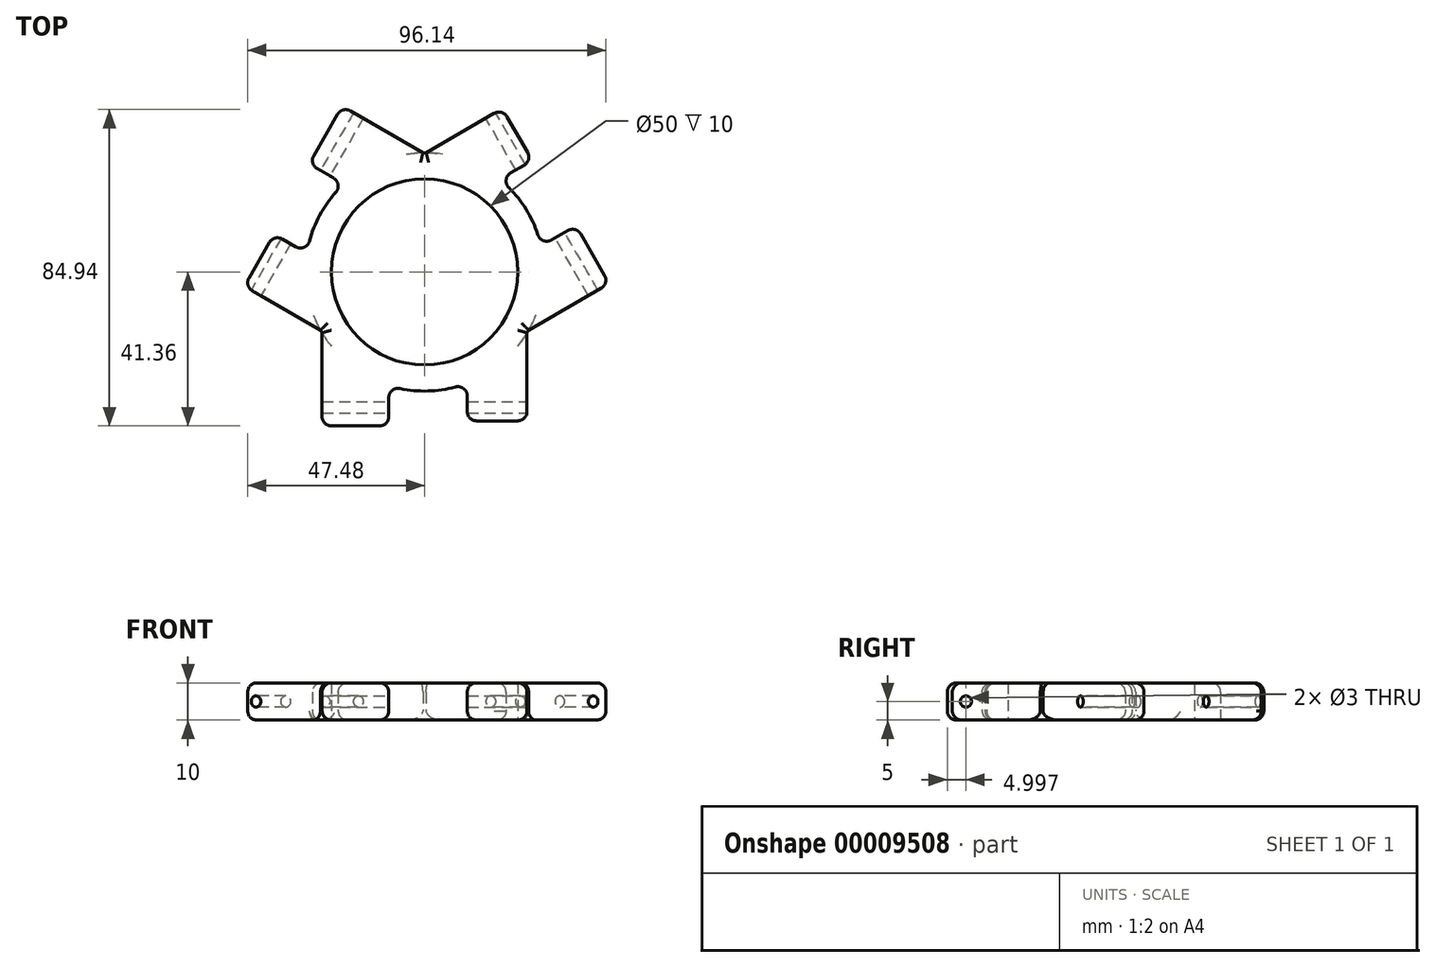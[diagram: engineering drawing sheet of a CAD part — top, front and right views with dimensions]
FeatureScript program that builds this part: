
annotation { "Feature Type Name" : "Feature", "Feature Type Description" : "" }
export const myFeature = defineFeature(function(context is Context, id is Id, definition is map)
    precondition{}
    {
        {
            var Q0;
            Q0=qCreatedBy(makeId("Top.planeOp"),FACE);
            var sketch = newSketch(context, id + "F0", { "sketchPlane" : qUnion([Q0])});
            skCircle(sketch, "E0", {"center": v(0, 0) * mm, "radius": 25 * mm});
            skCircle(sketch, "E1", {"center": v(0, 0) * mm, "radius": 32 * mm});
            skLineSegment(sketch, "E2", {"start": v(-9.6, -41.36) * mm, "end": v(-9.6, -30.53) * mm});
            skLineSegment(sketch, "E3", {"start": v(11.45, -29.88) * mm, "end": v(11.45, -40) * mm});
            skLineSegment(sketch, "E4", {"start": v(-27.5, -41.36) * mm, "end": v(-9.6, -41.36) * mm});
            skLineSegment(sketch, "E5", {"start": v(11.45, -40) * mm, "end": v(27.5, -40) * mm});
            skLineSegment(sketch, "E6", {"start": v(27.5, -40) * mm, "end": v(27.5, -16.36) * mm});
            skLineSegment(sketch, "E7", {"start": v(-27.5, -41.36) * mm, "end": v(-27.5, -16.36) * mm});
            skLineSegment(sketch, "E8.1.0", {"start": v(28.91, 29.92) * mm, "end": v(20.9, 43.82) * mm});
            skLineSegment(sketch, "E8.1.1", {"start": v(49.57, -3.13) * mm, "end": v(27.92, -15.63) * mm});
            skLineSegment(sketch, "E8.1.2", {"start": v(49.57, -3.13) * mm, "end": v(40.62, 12.37) * mm});
            skLineSegment(sketch, "E8.1.3", {"start": v(20.9, 43.82) * mm, "end": v(0.42, 32) * mm});
            skLineSegment(sketch, "E8.1.4", {"start": v(20.15, 24.86) * mm, "end": v(28.91, 29.92) * mm});
            skLineSegment(sketch, "E8.1.5", {"start": v(40.62, 12.37) * mm, "end": v(31.24, 6.95) * mm});
            skLineSegment(sketch, "E8.2.0", {"start": v(-40.37, 10.08) * mm, "end": v(-48.4, -3.82) * mm});
            skLineSegment(sketch, "E8.2.1", {"start": v(-22.07, 44.5) * mm, "end": v(-0.42, 32) * mm});
            skLineSegment(sketch, "E8.2.2", {"start": v(-22.07, 44.5) * mm, "end": v(-31.02, 29) * mm});
            skLineSegment(sketch, "E8.2.3", {"start": v(-48.4, -3.82) * mm, "end": v(-27.92, -15.63) * mm});
            skLineSegment(sketch, "E8.2.4", {"start": v(-31.6, 5.02) * mm, "end": v(-40.37, 10.08) * mm});
            skLineSegment(sketch, "E8.2.5", {"start": v(-31.02, 29) * mm, "end": v(-21.63, 23.58) * mm});
            skSolve(sketch);
        }
        {
            var Q0;
            Q0=makeQuery(id+"F0.imprint","IMPRINT",FACE,{"disambiguationData":[TD([[makeQuery(id+"F0.imprint","IMPRINT",EDGE,{"derivedFrom":sQuery(id+"F0.wireOp",EDGE,"E0")}),-1.0]])]});
            var Q1;
            Q1=makeQuery(id+"F0.imprint","IMPRINT",FACE,{"disambiguationData":[TD([[makeQuery(id+"F0.imprint","IMPRINT",EDGE,{"derivedFrom":sQuery(id+"F0.wireOp",EDGE,"E8.2.0")}),1.0]])]});
            var Q2;
            {var subQ1=sQuery(id+"F0.wireOp",EDGE,"E2");Q2=makeQuery(id+"F0.imprint","IMPRINT",FACE,{"disambiguationData":[TD([[makeQuery(id+"F0.imprint","IMPRINT",EDGE,{"derivedFrom":subQ1}),1.0]])]});}
            var Q3;
            {var subQ1=sQuery(id+"F0.wireOp",EDGE,"E8.2.1");Q3=makeQuery(id+"F0.imprint","IMPRINT",FACE,{"disambiguationData":[TD([[makeQuery(id+"F0.imprint","IMPRINT",EDGE,{"derivedFrom":subQ1}),-1.0]])]});}
            var Q4;
            Q4=makeQuery(id+"F0.imprint","IMPRINT",FACE,{"disambiguationData":[TD([[makeQuery(id+"F0.imprint","IMPRINT",EDGE,{"derivedFrom":sQuery(id+"F0.wireOp",EDGE,"E8.1.0")}),1.0]])]});
            var Q5;
            {var subQ1=sQuery(id+"F0.wireOp",EDGE,"E8.1.1");Q5=makeQuery(id+"F0.imprint","IMPRINT",FACE,{"disambiguationData":[TD([[makeQuery(id+"F0.imprint","IMPRINT",EDGE,{"derivedFrom":subQ1}),-1.0]])]});}
            var Q6;
            {var subQ0=sQuery(id+"F0.wireOp",EDGE,"E3");Q6=makeQuery(id+"F0.imprint","IMPRINT",FACE,{"disambiguationData":[TD([[makeQuery(id+"F0.imprint","IMPRINT",EDGE,{"derivedFrom":subQ0}),1.0]])]});}
            extrude(context, id + "F1", {"entities" : qUnion([Q0, Q1, Q2, Q3, Q4, Q5, Q6]), "depth" : 10 * mm});
        }
        {
            var Q0;
            Q0=makeQuery(id+"F1.opExtrude","SWEPT_FACE",FACE,{"disambiguationData":[OSD([sQuery(id+"F0.wireOp",EDGE,"E7")])]});
            var sketch = newSketch(context, id + "F2", { "sketchPlane" : qUnion([Q0])});
            skCircle(sketch, "E9", {"center": v(36.36, 5) * mm, "radius": 1.5 * mm});
            skSolve(sketch);
        }
        {
            var Q0;
            Q0 = qSketchRegion(id + "F2", true);
            extrude(context, id + "F3", {"entities" : qUnion([Q0]), "depth" : 5 * mm, "hasSecondDirection" : true, "secondDirectionOppositeDirection" : true, "secondDirectionDepth" : 60 * mm});
        }
        {
            var Q0;
            Q0=makeQuery(id+"F3.opExtrude","SWEPT_BODY",BODY,{"disambiguationData":[OSD([sQuery(id+"F2.wireOp",EDGE,"E9")])]});
            var Q1;
            Q1=makeQuery(id+"F1.opExtrude","SWEPT_FACE",FACE,{"disambiguationData":[OSD([sQuery(id+"F0.wireOp",EDGE,"E0")])]});
            circularPattern(context, id + "F4", {"entities" : qUnion([Q0]), "axis" : qUnion([Q1]), "angle" : 120 * degree, "instanceCount" : 3});
        }
        {
            var Q0;
            Q0=makeQuery(id+"F3.opExtrude","SWEPT_BODY",BODY,{"disambiguationData":[OSD([sQuery(id+"F2.wireOp",EDGE,"E9")])]});
            var Q1;
            Q1=makeQuery(id+"F4.opPattern","COPY",BODY,{"derivedFrom":makeQuery(id+"F3.opExtrude","SWEPT_BODY",BODY,{"disambiguationData":[OSD([sQuery(id+"F2.wireOp",EDGE,"E9")])]}),"instanceName":"2"});
            var Q2;
            Q2=makeQuery(id+"F4.opPattern","COPY",BODY,{"derivedFrom":makeQuery(id+"F3.opExtrude","SWEPT_BODY",BODY,{"disambiguationData":[OSD([sQuery(id+"F2.wireOp",EDGE,"E9")])]}),"instanceName":"1"});
            var Q3;
            Q3=makeQuery(id+"F1.opExtrude","SWEPT_BODY",BODY,{"disambiguationData":[OSD([sQuery(id+"F0.wireOp",EDGE,"E0"),sQuery(id+"F0.wireOp",EDGE,"E1"),sQuery(id+"F0.wireOp",EDGE,"E2"),sQuery(id+"F0.wireOp",EDGE,"E3"),sQuery(id+"F0.wireOp",EDGE,"E4"),sQuery(id+"F0.wireOp",EDGE,"E5"),sQuery(id+"F0.wireOp",EDGE,"E6"),sQuery(id+"F0.wireOp",EDGE,"E7"),sQuery(id+"F0.wireOp",EDGE,"E8.1.0"),sQuery(id+"F0.wireOp",EDGE,"E8.1.1"),sQuery(id+"F0.wireOp",EDGE,"E8.1.2"),sQuery(id+"F0.wireOp",EDGE,"E8.1.3"),sQuery(id+"F0.wireOp",EDGE,"E8.1.4"),sQuery(id+"F0.wireOp",EDGE,"E8.1.5"),sQuery(id+"F0.wireOp",EDGE,"E8.2.0"),sQuery(id+"F0.wireOp",EDGE,"E8.2.1"),sQuery(id+"F0.wireOp",EDGE,"E8.2.2"),sQuery(id+"F0.wireOp",EDGE,"E8.2.3"),sQuery(id+"F0.wireOp",EDGE,"E8.2.4"),sQuery(id+"F0.wireOp",EDGE,"E8.2.5")])]});
            booleanBodies(context, id + "F5", {"operationType" : BooleanOperationType.SUBTRACTION, "tools" : qUnion([Q0, Q1, Q2]), "targets" : qUnion([Q3])});
        }
        {
            var Q0;
            Q0=makeQuery(id+"F1.opExtrude","CAP_EDGE",EDGE,{"disambiguationData":[OSD([sQuery(id+"F0.wireOp",EDGE,"E8.2.3")])],"isStart":false});
            var Q1;
            Q1=makeQuery(id+"F1.opExtrude","CAP_EDGE",EDGE,{"disambiguationData":[OSD([sQuery(id+"F0.wireOp",EDGE,"E8.2.0")])],"isStart":false});
            var Q2;
            Q2=makeQuery(id+"F1.opExtrude","SWEPT_EDGE",EDGE,{"disambiguationData":[OSD([sQuery(id+"F0.wireOp",EDGE,"E8.2.0"),sQuery(id+"F0.wireOp",EDGE,"E8.2.3")])]});
            var Q3;
            Q3=makeQuery(id+"F1.opExtrude","CAP_EDGE",EDGE,{"disambiguationData":[OSD([sQuery(id+"F0.wireOp",EDGE,"E8.2.4")])],"isStart":false});
            var Q4;
            Q4=makeQuery(id+"F1.opExtrude","SWEPT_EDGE",EDGE,{"disambiguationData":[OSD([sQuery(id+"F0.wireOp",EDGE,"E8.2.0"),sQuery(id+"F0.wireOp",EDGE,"E8.2.4")])]});
            var Q5;
            Q5=makeQuery(id+"F1.opExtrude","CAP_EDGE",EDGE,{"disambiguationData":[OSD([sQuery(id+"F0.wireOp",EDGE,"E8.2.4")])],"isStart":true});
            var Q6;
            {var subQ0=sQuery(id+"F0.wireOp",EDGE,"E1");Q6=makeQuery(id+"F1.opExtrude","CAP_EDGE",EDGE,{"disambiguationData":[OSD([subQ0]),TDD([makeQuery(id+"F0.imprint","IMPRINT",EDGE,{"disambiguationData":[TD([[makeQuery(id+"F0.imprint","INTERSECT",VERTEX,{"derivedFrom":[subQ0,sQuery(id+"F0.wireOp",EDGE,"E8.2.4")]}),1.0]])],"derivedFrom":subQ0})])],"isStart":false});}
            var Q7;
            Q7=makeQuery(id+"F1.opExtrude","CAP_EDGE",EDGE,{"disambiguationData":[OSD([sQuery(id+"F0.wireOp",EDGE,"E8.2.5")])],"isStart":false});
            var Q8;
            Q8=makeQuery(id+"F1.opExtrude","CAP_EDGE",EDGE,{"disambiguationData":[OSD([sQuery(id+"F0.wireOp",EDGE,"E8.2.2")])],"isStart":false});
            var Q9;
            Q9=makeQuery(id+"F1.opExtrude","SWEPT_EDGE",EDGE,{"disambiguationData":[OSD([sQuery(id+"F0.wireOp",EDGE,"E8.2.2"),sQuery(id+"F0.wireOp",EDGE,"E8.2.5")])]});
            var Q10;
            Q10=makeQuery(id+"F1.opExtrude","SWEPT_EDGE",EDGE,{"disambiguationData":[OSD([sQuery(id+"F0.wireOp",EDGE,"E8.2.1"),sQuery(id+"F0.wireOp",EDGE,"E8.2.2")])]});
            var Q11;
            Q11=makeQuery(id+"F1.opExtrude","CAP_EDGE",EDGE,{"disambiguationData":[OSD([sQuery(id+"F0.wireOp",EDGE,"E8.2.1")])],"isStart":false});
            var Q12;
            Q12=makeQuery(id+"F1.opExtrude","CAP_EDGE",EDGE,{"disambiguationData":[OSD([sQuery(id+"F0.wireOp",EDGE,"E8.1.3")])],"isStart":false});
            var Q13;
            {var subQ0=sQuery(id+"F0.wireOp",EDGE,"E1");Q13=makeQuery(id+"F1.opExtrude","CAP_EDGE",EDGE,{"disambiguationData":[OSD([subQ0]),TDD([makeQuery(id+"F0.imprint","IMPRINT",EDGE,{"disambiguationData":[TD([[makeQuery(id+"F0.imprint","INTERSECT",VERTEX,{"derivedFrom":[subQ0,sQuery(id+"F0.wireOp",EDGE,"E8.1.4")]}),1.0]])],"derivedFrom":subQ0})])],"isStart":false});}
            var Q14;
            Q14=makeQuery(id+"F1.opExtrude","CAP_EDGE",EDGE,{"disambiguationData":[OSD([sQuery(id+"F0.wireOp",EDGE,"E8.1.0")])],"isStart":false});
            var Q15;
            Q15=makeQuery(id+"F1.opExtrude","CAP_EDGE",EDGE,{"disambiguationData":[OSD([sQuery(id+"F0.wireOp",EDGE,"E8.1.0")])],"isStart":true});
            var Q16;
            Q16=makeQuery(id+"F1.opExtrude","SWEPT_EDGE",EDGE,{"disambiguationData":[OSD([sQuery(id+"F0.wireOp",EDGE,"E8.1.0"),sQuery(id+"F0.wireOp",EDGE,"E8.1.3")])]});
            var Q17;
            Q17=makeQuery(id+"F1.opExtrude","CAP_EDGE",EDGE,{"disambiguationData":[OSD([sQuery(id+"F0.wireOp",EDGE,"E8.2.1")])],"isStart":true});
            var Q18;
            {var subQ0=sQuery(id+"F0.wireOp",EDGE,"E1");Q18=makeQuery(id+"F1.opExtrude","CAP_EDGE",EDGE,{"disambiguationData":[OSD([subQ0]),TDD([makeQuery(id+"F0.imprint","IMPRINT",EDGE,{"disambiguationData":[TD([[makeQuery(id+"F0.imprint","INTERSECT",VERTEX,{"derivedFrom":[subQ0,sQuery(id+"F0.wireOp",EDGE,"E8.1.4")]}),1.0]])],"derivedFrom":subQ0})])],"isStart":true});}
            var Q19;
            Q19=makeQuery(id+"F1.opExtrude","SWEPT_EDGE",EDGE,{"disambiguationData":[OSD([sQuery(id+"F0.wireOp",EDGE,"E8.1.0"),sQuery(id+"F0.wireOp",EDGE,"E8.1.4")])]});
            var Q20;
            Q20=makeQuery(id+"F1.opExtrude","CAP_EDGE",EDGE,{"disambiguationData":[OSD([sQuery(id+"F0.wireOp",EDGE,"E8.1.4")])],"isStart":false});
            var Q21;
            Q21=makeQuery(id+"F1.opExtrude","CAP_EDGE",EDGE,{"disambiguationData":[OSD([sQuery(id+"F0.wireOp",EDGE,"E8.1.5")])],"isStart":false});
            var Q22;
            Q22=makeQuery(id+"F1.opExtrude","CAP_EDGE",EDGE,{"disambiguationData":[OSD([sQuery(id+"F0.wireOp",EDGE,"E8.1.2")])],"isStart":false});
            var Q23;
            Q23=makeQuery(id+"F1.opExtrude","CAP_EDGE",EDGE,{"disambiguationData":[OSD([sQuery(id+"F0.wireOp",EDGE,"E8.1.2")])],"isStart":true});
            var Q24;
            Q24=makeQuery(id+"F1.opExtrude","SWEPT_EDGE",EDGE,{"disambiguationData":[OSD([sQuery(id+"F0.wireOp",EDGE,"E8.1.1"),sQuery(id+"F0.wireOp",EDGE,"E8.1.2")])]});
            var Q25;
            Q25=makeQuery(id+"F1.opExtrude","SWEPT_EDGE",EDGE,{"disambiguationData":[OSD([sQuery(id+"F0.wireOp",EDGE,"E8.1.2"),sQuery(id+"F0.wireOp",EDGE,"E8.1.5")])]});
            var Q26;
            Q26=makeQuery(id+"F1.opExtrude","CAP_EDGE",EDGE,{"disambiguationData":[OSD([sQuery(id+"F0.wireOp",EDGE,"E8.1.1")])],"isStart":false});
            var Q27;
            Q27=makeQuery(id+"F1.opExtrude","CAP_EDGE",EDGE,{"disambiguationData":[OSD([sQuery(id+"F0.wireOp",EDGE,"E8.1.1")])],"isStart":true});
            var Q28;
            Q28=makeQuery(id+"F1.opExtrude","CAP_EDGE",EDGE,{"disambiguationData":[OSD([sQuery(id+"F0.wireOp",EDGE,"E6")])],"isStart":false});
            var Q29;
            Q29=makeQuery(id+"F1.opExtrude","CAP_EDGE",EDGE,{"disambiguationData":[OSD([sQuery(id+"F0.wireOp",EDGE,"E6")])],"isStart":true});
            var Q30;
            Q30=makeQuery(id+"F1.opExtrude","SWEPT_EDGE",EDGE,{"disambiguationData":[OSD([sQuery(id+"F0.wireOp",EDGE,"E5"),sQuery(id+"F0.wireOp",EDGE,"E6")])]});
            var Q31;
            Q31=makeQuery(id+"F1.opExtrude","CAP_EDGE",EDGE,{"disambiguationData":[OSD([sQuery(id+"F0.wireOp",EDGE,"E5")])],"isStart":false});
            var Q32;
            Q32=makeQuery(id+"F1.opExtrude","CAP_EDGE",EDGE,{"disambiguationData":[OSD([sQuery(id+"F0.wireOp",EDGE,"E3")])],"isStart":false});
            var Q33;
            Q33=makeQuery(id+"F1.opExtrude","CAP_EDGE",EDGE,{"disambiguationData":[OSD([sQuery(id+"F0.wireOp",EDGE,"E5")])],"isStart":true});
            var Q34;
            Q34=makeQuery(id+"F1.opExtrude","SWEPT_EDGE",EDGE,{"disambiguationData":[OSD([sQuery(id+"F0.wireOp",EDGE,"E3"),sQuery(id+"F0.wireOp",EDGE,"E5")])]});
            var Q35;
            {var subQ0=sQuery(id+"F0.wireOp",EDGE,"E1");Q35=makeQuery(id+"F1.opExtrude","CAP_EDGE",EDGE,{"disambiguationData":[OSD([subQ0]),TDD([makeQuery(id+"F0.imprint","IMPRINT",EDGE,{"disambiguationData":[TD([[makeQuery(id+"F0.imprint","INTERSECT",VERTEX,{"derivedFrom":[subQ0,sQuery(id+"F0.wireOp",EDGE,"E2")]}),-1.0]])],"derivedFrom":subQ0})])],"isStart":false});}
            var Q36;
            {var subQ0=sQuery(id+"F0.wireOp",EDGE,"E1");Q36=makeQuery(id+"F1.opExtrude","CAP_EDGE",EDGE,{"disambiguationData":[OSD([subQ0]),TDD([makeQuery(id+"F0.imprint","IMPRINT",EDGE,{"disambiguationData":[TD([[makeQuery(id+"F0.imprint","INTERSECT",VERTEX,{"derivedFrom":[subQ0,sQuery(id+"F0.wireOp",EDGE,"E2")]}),-1.0]])],"derivedFrom":subQ0})])],"isStart":true});}
            var Q37;
            Q37=makeQuery(id+"F1.opExtrude","CAP_EDGE",EDGE,{"disambiguationData":[OSD([sQuery(id+"F0.wireOp",EDGE,"E2")])],"isStart":false});
            var Q38;
            Q38=makeQuery(id+"F1.opExtrude","CAP_EDGE",EDGE,{"disambiguationData":[OSD([sQuery(id+"F0.wireOp",EDGE,"E2")])],"isStart":true});
            var Q39;
            Q39=makeQuery(id+"F1.opExtrude","CAP_EDGE",EDGE,{"disambiguationData":[OSD([sQuery(id+"F0.wireOp",EDGE,"E4")])],"isStart":true});
            var Q40;
            Q40=makeQuery(id+"F1.opExtrude","CAP_EDGE",EDGE,{"disambiguationData":[OSD([sQuery(id+"F0.wireOp",EDGE,"E4")])],"isStart":false});
            var Q41;
            Q41=makeQuery(id+"F1.opExtrude","CAP_EDGE",EDGE,{"disambiguationData":[OSD([sQuery(id+"F0.wireOp",EDGE,"E7")])],"isStart":false});
            var Q42;
            Q42=makeQuery(id+"F1.opExtrude","CAP_EDGE",EDGE,{"disambiguationData":[OSD([sQuery(id+"F0.wireOp",EDGE,"E7")])],"isStart":true});
            var Q43;
            Q43=makeQuery(id+"F1.opExtrude","CAP_EDGE",EDGE,{"disambiguationData":[OSD([sQuery(id+"F0.wireOp",EDGE,"E8.2.3")])],"isStart":true});
            var Q44;
            Q44=makeQuery(id+"F1.opExtrude","CAP_EDGE",EDGE,{"disambiguationData":[OSD([sQuery(id+"F0.wireOp",EDGE,"E8.2.2")])],"isStart":true});
            var Q45;
            Q45=makeQuery(id+"F1.opExtrude","CAP_EDGE",EDGE,{"disambiguationData":[OSD([sQuery(id+"F0.wireOp",EDGE,"E8.2.5")])],"isStart":true});
            var Q46;
            Q46=makeQuery(id+"F1.opExtrude","CAP_EDGE",EDGE,{"disambiguationData":[OSD([sQuery(id+"F0.wireOp",EDGE,"E8.1.3")])],"isStart":true});
            var Q47;
            Q47=makeQuery(id+"F1.opExtrude","CAP_EDGE",EDGE,{"disambiguationData":[OSD([sQuery(id+"F0.wireOp",EDGE,"E3")])],"isStart":true});
            var Q48;
            Q48=makeQuery(id+"F1.opExtrude","CAP_EDGE",EDGE,{"disambiguationData":[OSD([sQuery(id+"F0.wireOp",EDGE,"E8.1.5")])],"isStart":true});
            var Q49;
            Q49=makeQuery(id+"F1.opExtrude","CAP_EDGE",EDGE,{"disambiguationData":[OSD([sQuery(id+"F0.wireOp",EDGE,"E8.1.4")])],"isStart":true});
            var Q50;
            {var subQ0=sQuery(id+"F0.wireOp",EDGE,"E1");Q50=makeQuery(id+"F1.opExtrude","CAP_EDGE",EDGE,{"disambiguationData":[OSD([subQ0]),TDD([makeQuery(id+"F0.imprint","IMPRINT",EDGE,{"disambiguationData":[TD([[makeQuery(id+"F0.imprint","INTERSECT",VERTEX,{"derivedFrom":[subQ0,sQuery(id+"F0.wireOp",EDGE,"E8.1.3")]}),-1.0]])],"derivedFrom":subQ0})])],"isStart":false});}
            var Q51;
            {var subQ0=sQuery(id+"F0.wireOp",EDGE,"E1");Q51=makeQuery(id+"F1.opExtrude","CAP_EDGE",EDGE,{"disambiguationData":[OSD([subQ0]),TDD([makeQuery(id+"F0.imprint","IMPRINT",EDGE,{"disambiguationData":[TD([[makeQuery(id+"F0.imprint","INTERSECT",VERTEX,{"derivedFrom":[subQ0,sQuery(id+"F0.wireOp",EDGE,"E7")]}),1.0]])],"derivedFrom":subQ0})])],"isStart":false});}
            var Q52;
            {var subQ0=sQuery(id+"F0.wireOp",EDGE,"E1");Q52=makeQuery(id+"F1.opExtrude","CAP_EDGE",EDGE,{"disambiguationData":[OSD([subQ0]),TDD([makeQuery(id+"F0.imprint","IMPRINT",EDGE,{"disambiguationData":[TD([[makeQuery(id+"F0.imprint","INTERSECT",VERTEX,{"derivedFrom":[subQ0,sQuery(id+"F0.wireOp",EDGE,"E6")]}),-1.0]])],"derivedFrom":subQ0})])],"isStart":false});}
            var Q53;
            Q53=makeQuery(id+"F1.opExtrude","CAP_EDGE",EDGE,{"disambiguationData":[OSD([sQuery(id+"F0.wireOp",EDGE,"E8.2.0")])],"isStart":true});
            var Q54;
            Q54=makeQuery(id+"F1.opExtrude","SWEPT_EDGE",EDGE,{"disambiguationData":[OSD([sQuery(id+"F0.wireOp",EDGE,"E4"),sQuery(id+"F0.wireOp",EDGE,"E7")])]});
            var Q55;
            Q55=makeQuery(id+"F1.opExtrude","SWEPT_EDGE",EDGE,{"disambiguationData":[OSD([sQuery(id+"F0.wireOp",EDGE,"E2"),sQuery(id+"F0.wireOp",EDGE,"E4")])]});
            var Q56;
            Q56=makeQuery(id+"F1.opExtrude","SWEPT_EDGE",EDGE,{"disambiguationData":[OSD([sQuery(id+"F0.wireOp",EDGE,"E1"),sQuery(id+"F0.wireOp",EDGE,"E8.1.5")])]});
            var Q57;
            Q57=makeQuery(id+"F1.opExtrude","SWEPT_EDGE",EDGE,{"disambiguationData":[OSD([sQuery(id+"F0.wireOp",EDGE,"E1"),sQuery(id+"F0.wireOp",EDGE,"E8.1.4")])]});
            var Q58;
            Q58=makeQuery(id+"F1.opExtrude","SWEPT_EDGE",EDGE,{"disambiguationData":[OSD([sQuery(id+"F0.wireOp",EDGE,"E1"),sQuery(id+"F0.wireOp",EDGE,"E8.2.5")])]});
            var Q59;
            Q59=makeQuery(id+"F1.opExtrude","SWEPT_EDGE",EDGE,{"disambiguationData":[OSD([sQuery(id+"F0.wireOp",EDGE,"E1"),sQuery(id+"F0.wireOp",EDGE,"E8.2.4")])]});
            var Q60;
            Q60=makeQuery(id+"F1.opExtrude","SWEPT_EDGE",EDGE,{"disambiguationData":[OSD([sQuery(id+"F0.wireOp",EDGE,"E1"),sQuery(id+"F0.wireOp",EDGE,"E2")])]});
            var Q61;
            Q61=makeQuery(id+"F1.opExtrude","SWEPT_EDGE",EDGE,{"disambiguationData":[OSD([sQuery(id+"F0.wireOp",EDGE,"E1"),sQuery(id+"F0.wireOp",EDGE,"E3")])]});
            fillet(context, id + "F6", {"entities" : qUnion([Q0, Q1, Q2, Q3, Q4, Q5, Q6, Q7, Q8, Q9, Q10, Q11, Q12, Q13, Q14, Q15, Q16, Q17, Q18, Q19, Q20, Q21, Q22, Q23, Q24, Q25, Q26, Q27, Q28, Q29, Q30, Q31, Q32, Q33, Q34, Q35, Q36, Q37, Q38, Q39, Q40, Q41, Q42, Q43, Q44, Q45, Q46, Q47, Q48, Q49, Q50, Q51, Q52, Q53, Q54, Q55, Q56, Q57, Q58, Q59, Q60, Q61]), "radius" : 2.5 * mm, "tangentPropagation" : true, "allowEdgeOverflow" : false});
        }
    });
